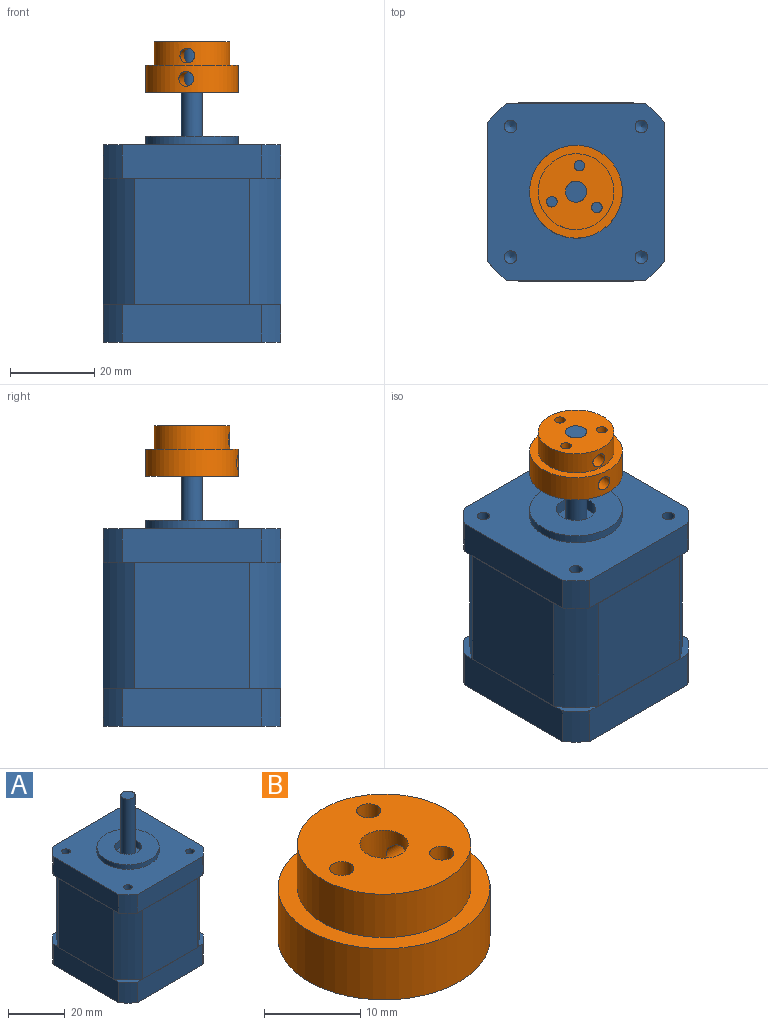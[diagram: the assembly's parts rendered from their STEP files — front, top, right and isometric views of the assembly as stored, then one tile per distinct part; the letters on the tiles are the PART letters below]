
ASSEMBLY  parts=2 mates=1
PART A: 56 faces, bbox 42.2x42.2x71.2 mm
  f0: plane 27.68x0.1mm, normal (0,0,-1), area 2.8mm2, adj f25,f26,f27,f33
  f1: plane 27.68x0.1mm, normal (0,0,-1), area 2.8mm2, adj f20,f21,f27,f35
  f2: plane 27.68x0.1mm, normal (0,0,-1), area 2.8mm2, adj f23,f24,f25,f39
  f3: plane 7.16x7.16mm, normal (0,0,-1), area 12.8mm2, adj f9,f10,f11,f21
  f4: plane 7.16x7.16mm, normal (0,0,-1), area 12.8mm2, adj f11,f12,f13,f23
  f5: plane 7.16x7.16mm, normal (0,0,-1), area 12.8mm2, adj f7,f13,f14,f25
  f6: plane 7.16x7.16mm, normal (0,0,-1), area 12.8mm2, adj f7,f8,f9,f27
  f7: plane 32.98x8mm, normal (1,0,0), area 263.8mm2, adj f5,f6,f8,f14,f15,f18
  f8: cylinder r=26.7mm len=8mm, axis (0,0,1), area 51.2mm2, adj f6,f7,f9,f15
  f9: plane 32.98x8mm, normal (0,1,0), area 263.8mm2, adj f3,f6,f8,f10,f15,f19
  f10: cylinder r=26.7mm len=8mm, axis (0,0,1), area 51.2mm2, adj f3,f9,f11,f15
  f11: plane 32.98x8mm, normal (-1,0,0), area 263.8mm2, adj f3,f4,f10,f12,f15,f17
  f12: cylinder r=26.7mm len=8mm, axis (0,0,1), area 51.2mm2, adj f4,f11,f13,f15
  f13: plane 32.98x8mm, normal (0,-1,0), area 263.8mm2, adj f4,f5,f12,f14,f15,f16
  f14: cylinder r=26.7mm len=8mm, axis (0,0,1), area 51.2mm2, adj f5,f7,f13,f15
  f15: plane 42x42mm, normal (0,0,1), area 1318.2mm2, adj f7,f8,f9,f10,f11,f12,f13,f14
  f16: plane 27.68x0.1mm, normal (0,0,1), area 2.8mm2, adj f13,f23,f24,f25
  f17: plane 27.68x0.1mm, normal (0,0,1), area 2.8mm2, adj f11,f21,f22,f23
  f18: plane 27.68x0.1mm, normal (0,0,1), area 2.8mm2, adj f7,f25,f26,f27
  f19: plane 27.68x0.1mm, normal (0,0,1), area 2.8mm2, adj f9,f20,f21,f27
  f20: plane 29.9x27.37mm, normal (0,1,0), area 818.4mm2, adj f1,f19,f21,f27
  f21: cylinder r=25.15mm len=29.9mm, axis (0,0,-1), area 315.8mm2, adj f1,f3,f17,f19,f20,f22,f28,f32
  f22: plane 29.9x27.37mm, normal (-1,0,0), area 818.4mm2, adj f17,f21,f23,f28
  f23: cylinder r=25.15mm len=29.9mm, axis (0,0,-1), area 315.8mm2, adj f2,f4,f16,f17,f22,f24,f28,f31
  f24: plane 29.9x27.37mm, normal (0,-1,0), area 818.4mm2, adj f2,f16,f23,f25
  f25: cylinder r=25.15mm len=29.9mm, axis (0,0,-1), area 315.8mm2, adj f0,f2,f5,f16,f18,f24,f26,f30
  f26: plane 29.9x27.37mm, normal (1,0,0), area 818.4mm2, adj f0,f18,f25,f27
  f27: cylinder r=25.15mm len=29.9mm, axis (0,0,-1), area 315.8mm2, adj f0,f1,f6,f18,f19,f20,f26,f29
  f28: plane 27.68x0.1mm, normal (0,0,-1), area 2.8mm2, adj f21,f22,f23,f37
  f29: plane 7.16x7.16mm, normal (0,0,1), area 12.8mm2, adj f27,f33,f34,f35
  f30: plane 7.16x7.16mm, normal (0,0,1), area 12.8mm2, adj f25,f33,f39,f40
  f31: plane 7.16x7.16mm, normal (0,0,1), area 12.8mm2, adj f23,f37,f38,f39
  f32: plane 7.16x7.16mm, normal (0,0,1), area 12.8mm2, adj f21,f35,f36,f37
  f33: plane 32.98x8.9mm, normal (1,0,0), area 293.5mm2, adj f0,f29,f30,f34,f40,f41
  f34: cylinder r=26.7mm len=8.9mm, axis (0,0,1), area 56.9mm2, adj f29,f33,f35,f41
  f35: plane 32.98x8.9mm, normal (0,1,0), area 293.5mm2, adj f1,f29,f32,f34,f36,f41
  f36: cylinder r=26.7mm len=8.9mm, axis (0,0,1), area 56.9mm2, adj f32,f35,f37,f41
  f37: plane 32.98x8.9mm, normal (-1,0,0), area 293.5mm2, adj f28,f31,f32,f36,f38,f41
  f38: cylinder r=26.7mm len=8.9mm, axis (0,0,1), area 56.9mm2, adj f31,f37,f39,f41
  f39: plane 32.98x8.9mm, normal (0,-1,0), area 293.5mm2, adj f2,f30,f31,f38,f40,f41
  f40: cylinder r=26.7mm len=8.9mm, axis (0,0,1), area 56.9mm2, adj f30,f33,f39,f41
  f41: plane 42x42mm, normal (0,0,-1), area 1726.6mm2, adj f33,f34,f35,f36,f37,f38,f39,f40
  f42: cylinder r=4.7mm len=9.4mm, axis (0,0,-1), area 88.6mm2, adj f44,f45
  f43: cylinder r=11mm len=22mm, axis (0,0,-1), area 138.2mm2, adj f15,f44
  f44: plane 22x22mm, normal (0,0,1), area 310.7mm2, adj f42,f43
  f45: plane 9.4x9.4mm, normal (0,0,1), area 49.8mm2, adj f42,f47
  f46: plane 5x5mm, normal (0,0,1), area 19.6mm2, adj f47
  f47: cylinder r=2.5mm len=25.4mm, axis (0,0,-1), area 399mm2, adj f45,f46
  f48: cylinder r=1.5mm len=5mm, axis (0,0,1), area 47.1mm2, adj f15,f49
  f49: cone r=0mm half-angle=59deg, axis (0,0,1), area 8.2mm2, adj f48
  f50: cylinder r=1.5mm len=5mm, axis (0,0,1), area 47.1mm2, adj f15,f51
  f51: cone r=0mm half-angle=59deg, axis (0,0,1), area 8.2mm2, adj f50
  f52: cylinder r=1.5mm len=5mm, axis (0,0,1), area 47.1mm2, adj f15,f53
  f53: cone r=0mm half-angle=59deg, axis (0,0,1), area 8.2mm2, adj f52
  f54: cylinder r=1.5mm len=5mm, axis (0,0,1), area 47.1mm2, adj f15,f55
  f55: cone r=0mm half-angle=59deg, axis (0,0,1), area 8.2mm2, adj f54
PART B: 15 faces, bbox 22x22x12 mm
  f0: cylinder r=11mm len=22mm, axis (0,0,-1), area 439.6mm2, adj f3,f4,f13
  f1: cylinder r=2.5mm len=12mm, axis (0,0,-1), area 168.7mm2, adj f4,f5,f9,f10,f11,f12,f13,f14
  f2: cylinder r=9mm len=18mm, axis (0,0,-1), area 301.4mm2, adj f3,f5,f10
  f3: plane 22x22mm, normal (0,0,1), area 125.7mm2, adj f0,f2
  f4: plane 22x22mm, normal (0,0,-1), area 345.8mm2, adj f0,f1,f6,f7,f8
  f5: plane 18x18mm, normal (0,0,1), area 220.1mm2, adj f1,f2,f6,f7,f8
  f6: cylinder r=1.25mm len=12mm, axis (0,0,-1), area 94.2mm2, adj f4,f5
  f7: cylinder r=1.25mm len=12mm, axis (0,0,-1), area 94.2mm2, adj f4,f5
  f8: cylinder r=1.25mm len=12mm, axis (0,0,-1), area 94.2mm2, adj f4,f5
  f9: cone r=0mm half-angle=59deg, axis (1,0,0), area 0.2mm2, adj f1,f10
  f10: cylinder r=1.75mm len=7mm, axis (1,0,0), area 73.8mm2, adj f1,f2,f9,f11
  f11: cone r=0mm half-angle=59deg, axis (1,0,0), area 0.2mm2, adj f1,f10
  f12: cone r=0mm half-angle=59deg, axis (1,0,0), area 0.2mm2, adj f1,f13
  f13: cylinder r=1.75mm len=9mm, axis (1,0,0), area 95.9mm2, adj f0,f1,f12,f14
  f14: cone r=0mm half-angle=59deg, axis (1,0,0), area 0.2mm2, adj f1,f13
PLACE A t=(0,0,-2)mm fixed
PLACE B rot(axis=(0,0,-1),97.3deg) t=(0,0,3.4)mm
MATE revolute B.f1 <-> A.f8  axis (0,0,-1) through (0,0,3.4)mm
